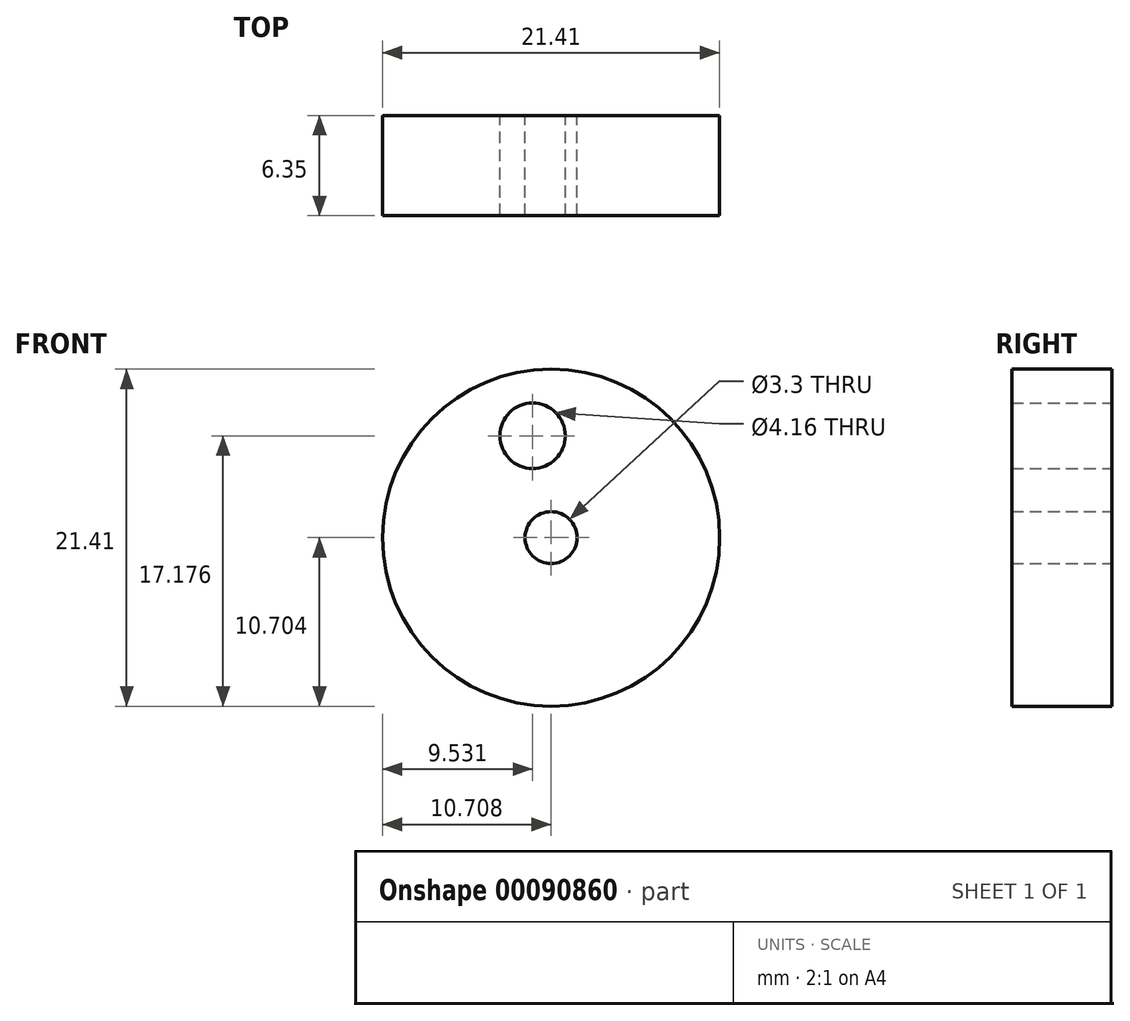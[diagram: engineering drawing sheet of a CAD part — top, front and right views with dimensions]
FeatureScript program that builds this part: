
annotation { "Feature Type Name" : "Feature", "Feature Type Description" : "" }
export const myFeature = defineFeature(function(context is Context, id is Id, definition is map)
    precondition{}
    {
        {
            var Q0;
            Q0=qCreatedBy(makeId("Front.planeOp"),FACE);
            var sketch = newSketch(context, id + "F0", { "sketchPlane" : qUnion([Q0])});
            skCircle(sketch, "E0", {"center": v(-29.56, 15.88) * mm, "radius": 10.7 * mm});
            skCircle(sketch, "E1", {"center": v(-29.56, 15.88) * mm, "radius": 1.65 * mm});
            skCircle(sketch, "E2", {"center": v(-30.74, 22.36) * mm, "radius": 2.08 * mm});
            skSolve(sketch);
        }
        {
            var Q0;
            Q0=makeQuery(id+"F0.imprint","IMPRINT",FACE,{"disambiguationData":[TD([[makeQuery(id+"F0.imprint","IMPRINT",EDGE,{"derivedFrom":sQuery(id+"F0.wireOp",EDGE,"E0")}),1.0]])]});
            extrude(context, id + "F1", {"entities" : qUnion([Q0]), "depth" : 6.35 * mm});
        }
    });
